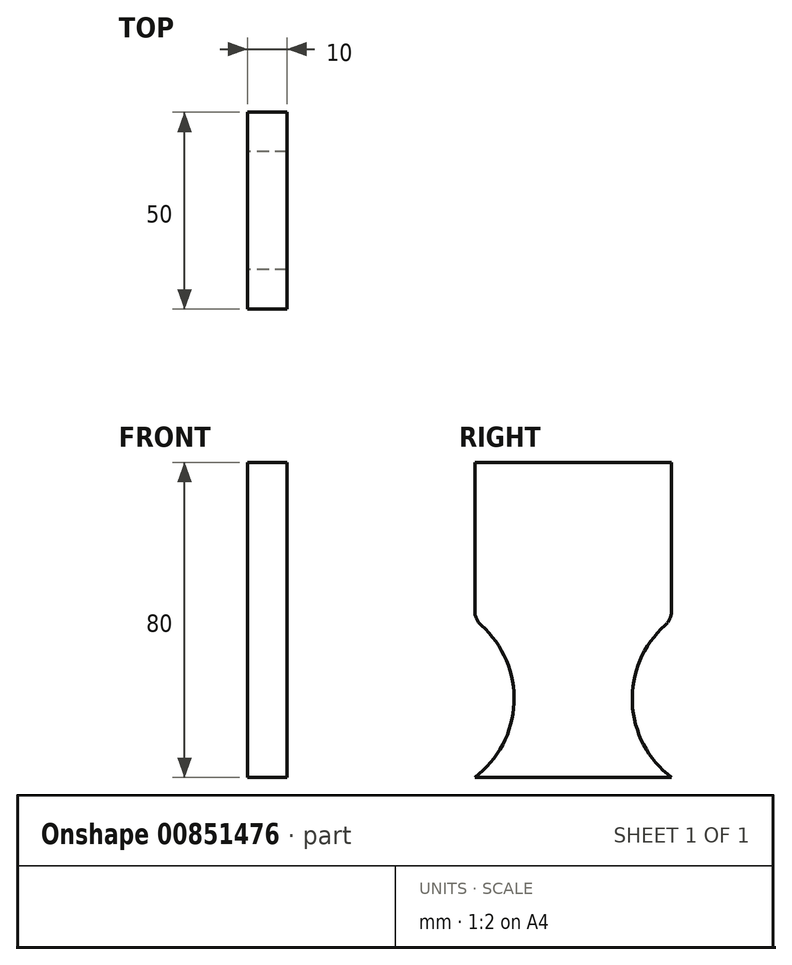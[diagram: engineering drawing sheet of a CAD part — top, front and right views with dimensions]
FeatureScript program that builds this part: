
annotation { "Feature Type Name" : "Feature", "Feature Type Description" : "" }
export const myFeature = defineFeature(function(context is Context, id is Id, definition is map)
    precondition{}
    {
        {
            var Q0;
            Q0=qCreatedBy(makeId("Right.planeOp"),FACE);
            var sketch = newSketch(context, id + "F0", { "sketchPlane" : qUnion([Q0])});
            skLineSegment(sketch, "E0", {"start": v(44.23, 60.61) * mm, "end": v(44.23, 22.98) * mm});
            skLineSegment(sketch, "E1", {"start": v(44.23, 60.61) * mm, "end": v(-5.77, 60.61) * mm});
            skLineSegment(sketch, "E2", {"start": v(-5.77, 60.61) * mm, "end": v(-5.77, 22.98) * mm});
            skLineSegment(sketch, "E3", {"start": v(-5.77, -19.39) * mm, "end": v(44.23, -19.39) * mm});
            skArc(sketch, "E4", {"start": v(42.56, 19.25) * mm, "mid": v(34.25, -0.46) * mm, "end": v(44.23, -19.39) * mm});
            skArc(sketch, "E5", {"start": v(-5.77, -19.39) * mm, "mid": v(4.2, -0.46) * mm, "end": v(-4.1, 19.25) * mm});
            skPoint(sketch, "E6.newPointA", {"position": v(44.23, -19.39) * mm});
            skPoint(sketch, "E6.newPointB", {"position": v(44.23, 20.61) * mm});
            skArc(sketch, "E6.filletArc", {"start": v(42.56, 19.25) * mm, "mid": v(43.8, 20.93) * mm, "end": v(44.23, 22.98) * mm});
            skPoint(sketch, "E7.newPointA", {"position": v(-5.77, 20.61) * mm});
            skPoint(sketch, "E7.newPointB", {"position": v(-5.77, -19.39) * mm});
            skArc(sketch, "E7.filletArc", {"start": v(-5.77, 22.98) * mm, "mid": v(-5.34, 20.93) * mm, "end": v(-4.1, 19.25) * mm});
            skSolve(sketch);
        }
        {
            var Q0;
            Q0 = qSketchRegion(id + "F0", true);
            extrude(context, id + "F1", {"entities" : qUnion([Q0]), "depth" : 10 * mm, "offsetDistance" : 25 * mm});
        }
    });
